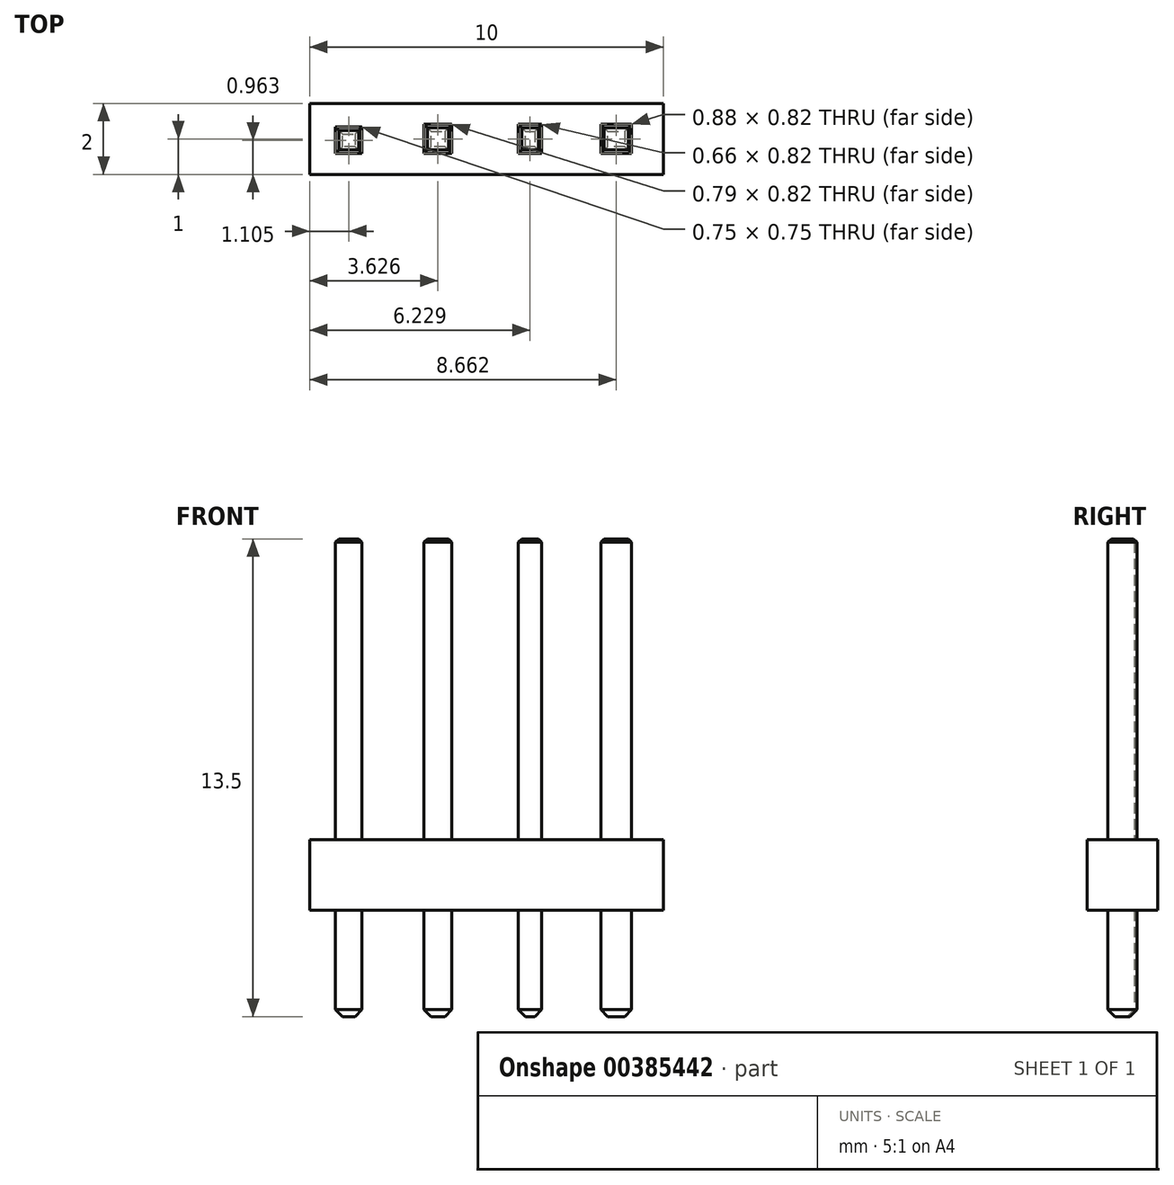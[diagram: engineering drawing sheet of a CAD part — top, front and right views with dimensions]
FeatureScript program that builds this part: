
annotation { "Feature Type Name" : "Feature", "Feature Type Description" : "" }
export const myFeature = defineFeature(function(context is Context, id is Id, definition is map)
    precondition{}
    {
        {
            var Q0;
            Q0=qCreatedBy(makeId("Top.planeOp"),FACE);
            var sketch = newSketch(context, id + "F0", { "sketchPlane" : qUnion([Q0])});
            skLineSegment(sketch, "E0.bottom", {"start": v(5, -1) * mm, "end": v(-5, -1) * mm});
            skLineSegment(sketch, "E0.top", {"start": v(5, 1) * mm, "end": v(-5, 1) * mm});
            skLineSegment(sketch, "E0.left", {"start": v(5, -1) * mm, "end": v(5, 1) * mm});
            skLineSegment(sketch, "E0.right", {"start": v(-5, -1) * mm, "end": v(-5, 1) * mm});
            skPoint(sketch, "E0.middle", {"position": v(0, 0) * mm});
            skSolve(sketch);
        }
        {
            var Q0;
            Q0=makeQuery(id+"F0.imprint","IMPRINT",FACE,{"disambiguationData":[TD([[makeQuery(id+"F0.imprint","IMPRINT",EDGE,{"derivedFrom":sQuery(id+"F0.wireOp",EDGE,"E0.bottom")}),-1.0]])]});
            extrude(context, id + "F1", {"entities" : qUnion([Q0]), "depth" : 2 * mm});
        }
        {
            var Q0;
            Q0=makeQuery(id+"F1.opExtrude","CAP_FACE",FACE,{"disambiguationData":[OSD([sQuery(id+"F0.wireOp",EDGE,"E0.bottom"),sQuery(id+"F0.wireOp",EDGE,"E0.top"),sQuery(id+"F0.wireOp",EDGE,"E0.left"),sQuery(id+"F0.wireOp",EDGE,"E0.right")])],"isStart":false});
            var sketch = newSketch(context, id + "F2", { "sketchPlane" : qUnion([Q0])});
            skLineSegment(sketch, "E1.bottom", {"start": v(-3.52, -0.41) * mm, "end": v(-4.27, -0.41) * mm});
            skLineSegment(sketch, "E1.top", {"start": v(-3.52, 0.34) * mm, "end": v(-4.27, 0.34) * mm});
            skLineSegment(sketch, "E1.left", {"start": v(-3.52, -0.41) * mm, "end": v(-3.52, 0.34) * mm});
            skLineSegment(sketch, "E1.right", {"start": v(-4.27, -0.41) * mm, "end": v(-4.27, 0.34) * mm});
            skLineSegment(sketch, "E2.bottom", {"start": v(-1.77, -0.41) * mm, "end": v(-0.98, -0.41) * mm});
            skLineSegment(sketch, "E2.top", {"start": v(-1.77, 0.41) * mm, "end": v(-0.98, 0.41) * mm});
            skLineSegment(sketch, "E2.left", {"start": v(-1.77, -0.41) * mm, "end": v(-1.77, 0.41) * mm});
            skLineSegment(sketch, "E2.right", {"start": v(-0.98, -0.41) * mm, "end": v(-0.98, 0.41) * mm});
            skPoint(sketch, "E2.middle", {"position": v(-1.37, 0) * mm});
            skLineSegment(sketch, "E3.bottom", {"start": v(0.9, -0.41) * mm, "end": v(1.56, -0.41) * mm});
            skLineSegment(sketch, "E3.top", {"start": v(0.9, 0.41) * mm, "end": v(1.56, 0.41) * mm});
            skLineSegment(sketch, "E3.left", {"start": v(0.9, -0.41) * mm, "end": v(0.9, 0.41) * mm});
            skLineSegment(sketch, "E3.right", {"start": v(1.56, -0.41) * mm, "end": v(1.56, 0.41) * mm});
            skPoint(sketch, "E3.middle", {"position": v(1.23, 0) * mm});
            skLineSegment(sketch, "E4.bottom", {"start": v(3.22, -0.41) * mm, "end": v(4.1, -0.41) * mm});
            skLineSegment(sketch, "E4.top", {"start": v(3.22, 0.41) * mm, "end": v(4.1, 0.41) * mm});
            skLineSegment(sketch, "E4.left", {"start": v(3.22, -0.41) * mm, "end": v(3.22, 0.41) * mm});
            skLineSegment(sketch, "E4.right", {"start": v(4.1, -0.41) * mm, "end": v(4.1, 0.41) * mm});
            skPoint(sketch, "E4.middle", {"position": v(3.66, 0) * mm});
            skSolve(sketch);
        }
        {
            var Q0;
            Q0=makeQuery(id+"F2.imprint","IMPRINT",FACE,{"disambiguationData":[TD([[makeQuery(id+"F2.imprint","IMPRINT",EDGE,{"derivedFrom":sQuery(id+"F2.wireOp",EDGE,"E1.bottom")}),-1.0]])]});
            var Q1;
            Q1=makeQuery(id+"F2.imprint","IMPRINT",FACE,{"disambiguationData":[TD([[makeQuery(id+"F2.imprint","IMPRINT",EDGE,{"derivedFrom":sQuery(id+"F2.wireOp",EDGE,"E2.bottom")}),1.0]])]});
            var Q2;
            Q2=makeQuery(id+"F2.imprint","IMPRINT",FACE,{"disambiguationData":[TD([[makeQuery(id+"F2.imprint","IMPRINT",EDGE,{"derivedFrom":sQuery(id+"F2.wireOp",EDGE,"E3.bottom")}),1.0]])]});
            var Q3;
            Q3=makeQuery(id+"F2.imprint","IMPRINT",FACE,{"disambiguationData":[TD([[makeQuery(id+"F2.imprint","IMPRINT",EDGE,{"derivedFrom":sQuery(id+"F2.wireOp",EDGE,"E4.bottom")}),1.0]])]});
            extrude(context, id + "F3", {"entities" : qUnion([Q0, Q1, Q2, Q3]), "operationType" : NewBodyOperationType.ADD, "depth" : 8.5 * mm, "hasSecondDirection" : true, "secondDirectionOppositeDirection" : true, "secondDirectionDepth" : 5 * mm});
        }
        {
            var Q0;
            Q0=makeQuery(id+"F3.opExtrude","CAP_EDGE",EDGE,{"disambiguationData":[OSD([sQuery(id+"F2.wireOp",EDGE,"E1.bottom")])],"isStart":false});
            var Q1;
            Q1=makeQuery(id+"F3.opExtrude","CAP_EDGE",EDGE,{"disambiguationData":[OSD([sQuery(id+"F2.wireOp",EDGE,"E1.left")])],"isStart":false});
            var Q2;
            Q2=makeQuery(id+"F3.opExtrude","CAP_EDGE",EDGE,{"disambiguationData":[OSD([sQuery(id+"F2.wireOp",EDGE,"E1.top")])],"isStart":false});
            var Q3;
            Q3=makeQuery(id+"F3.opExtrude","CAP_EDGE",EDGE,{"disambiguationData":[OSD([sQuery(id+"F2.wireOp",EDGE,"E1.right")])],"isStart":false});
            chamfer(context, id + "F4", {"entities" : qUnion([Q0, Q1, Q2, Q3]), "width" : 0.1 * mm, "tangentPropagation" : true});
        }
        {
            var Q0;
            Q0=makeQuery(id+"F3.opExtrude","CAP_EDGE",EDGE,{"disambiguationData":[OSD([sQuery(id+"F2.wireOp",EDGE,"E2.bottom")])],"isStart":false});
            var Q1;
            Q1=makeQuery(id+"F3.opExtrude","CAP_EDGE",EDGE,{"disambiguationData":[OSD([sQuery(id+"F2.wireOp",EDGE,"E2.right")])],"isStart":false});
            var Q2;
            Q2=makeQuery(id+"F3.opExtrude","CAP_EDGE",EDGE,{"disambiguationData":[OSD([sQuery(id+"F2.wireOp",EDGE,"E2.top")])],"isStart":false});
            var Q3;
            Q3=makeQuery(id+"F3.opExtrude","CAP_EDGE",EDGE,{"disambiguationData":[OSD([sQuery(id+"F2.wireOp",EDGE,"E2.left")])],"isStart":false});
            chamfer(context, id + "F5", {"entities" : qUnion([Q0, Q1, Q2, Q3]), "width" : 0.1 * mm, "tangentPropagation" : true});
        }
        {
            var Q0;
            Q0=makeQuery(id+"F3.opExtrude","CAP_FACE",FACE,{"disambiguationData":[OSD([sQuery(id+"F2.wireOp",EDGE,"E3.bottom"),sQuery(id+"F2.wireOp",EDGE,"E3.top"),sQuery(id+"F2.wireOp",EDGE,"E3.left"),sQuery(id+"F2.wireOp",EDGE,"E3.right")])],"isStart":false});
            chamfer(context, id + "F6", {"entities" : qUnion([Q0]), "width" : 0.1 * mm, "tangentPropagation" : true});
        }
        {
            var Q0;
            Q0=makeQuery(id+"F3.opExtrude","CAP_FACE",FACE,{"disambiguationData":[OSD([sQuery(id+"F2.wireOp",EDGE,"E4.bottom"),sQuery(id+"F2.wireOp",EDGE,"E4.top"),sQuery(id+"F2.wireOp",EDGE,"E4.left"),sQuery(id+"F2.wireOp",EDGE,"E4.right")])],"isStart":false});
            chamfer(context, id + "F7", {"entities" : qUnion([Q0]), "width" : 0.1 * mm, "tangentPropagation" : true});
        }
        {
            var Q0;
            Q0=makeQuery(id+"F3.opExtrude","CAP_FACE",FACE,{"disambiguationData":[OSD([sQuery(id+"F2.wireOp",EDGE,"E4.bottom"),sQuery(id+"F2.wireOp",EDGE,"E4.top"),sQuery(id+"F2.wireOp",EDGE,"E4.left"),sQuery(id+"F2.wireOp",EDGE,"E4.right")])],"isStart":true});
            var Q1;
            Q1=makeQuery(id+"F3.opExtrude","CAP_FACE",FACE,{"disambiguationData":[OSD([sQuery(id+"F2.wireOp",EDGE,"E3.bottom"),sQuery(id+"F2.wireOp",EDGE,"E3.top"),sQuery(id+"F2.wireOp",EDGE,"E3.left"),sQuery(id+"F2.wireOp",EDGE,"E3.right")])],"isStart":true});
            var Q2;
            Q2=makeQuery(id+"F3.opExtrude","CAP_FACE",FACE,{"disambiguationData":[OSD([sQuery(id+"F2.wireOp",EDGE,"E2.bottom"),sQuery(id+"F2.wireOp",EDGE,"E2.top"),sQuery(id+"F2.wireOp",EDGE,"E2.left"),sQuery(id+"F2.wireOp",EDGE,"E2.right")])],"isStart":true});
            var Q3;
            Q3=makeQuery(id+"F3.opExtrude","CAP_FACE",FACE,{"disambiguationData":[OSD([sQuery(id+"F2.wireOp",EDGE,"E1.bottom"),sQuery(id+"F2.wireOp",EDGE,"E1.top"),sQuery(id+"F2.wireOp",EDGE,"E1.left"),sQuery(id+"F2.wireOp",EDGE,"E1.right")])],"isStart":true});
            chamfer(context, id + "F8", {"entities" : qUnion([Q0, Q1, Q2, Q3]), "width" : 0.2 * mm, "tangentPropagation" : true});
        }
    });
